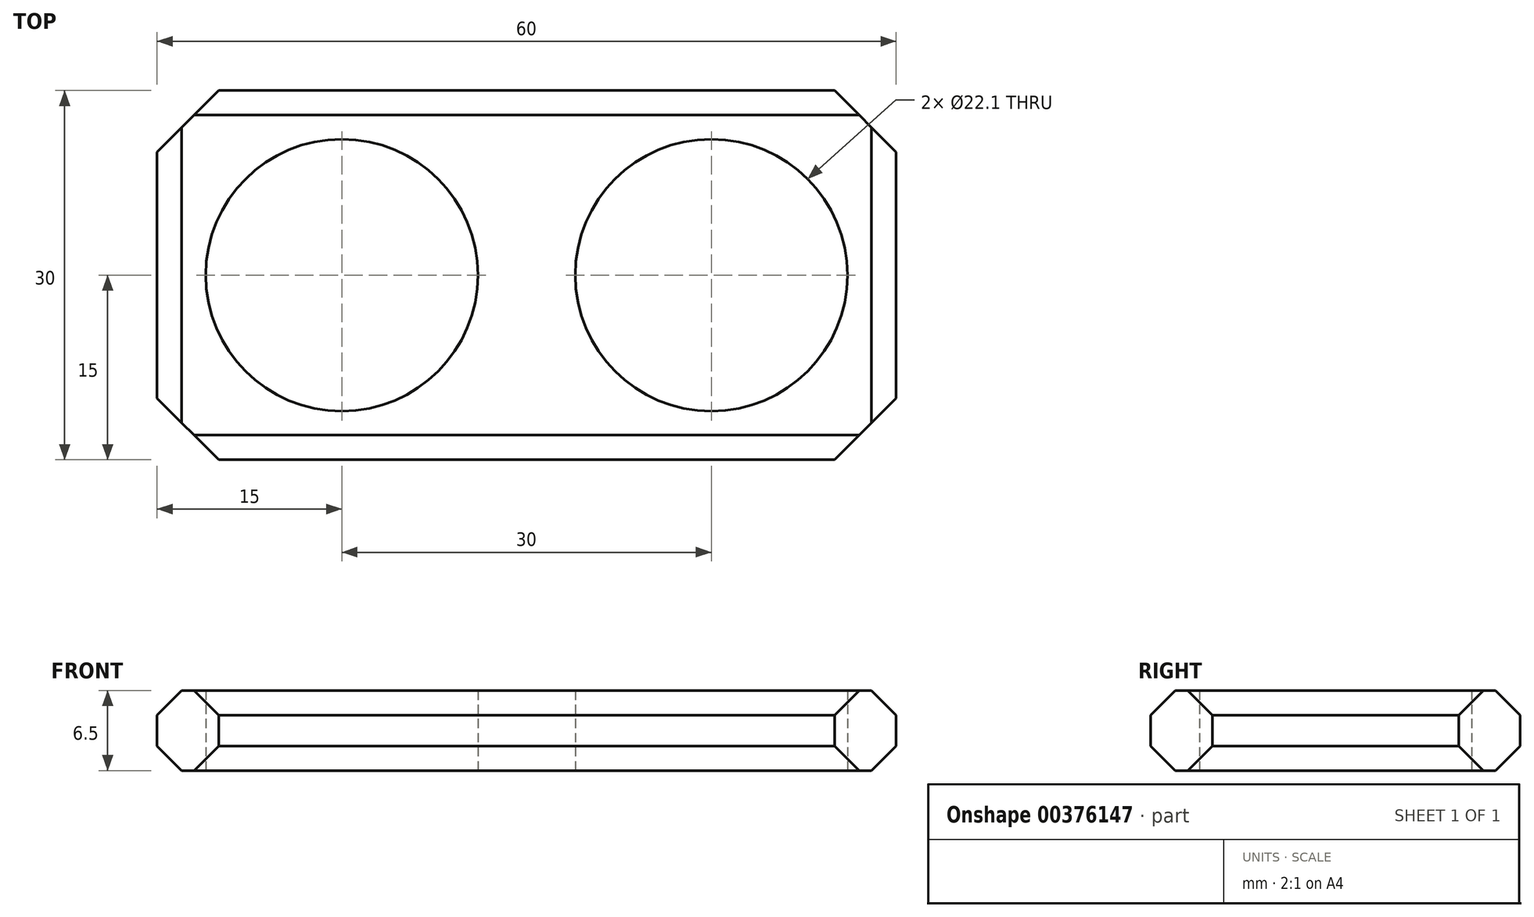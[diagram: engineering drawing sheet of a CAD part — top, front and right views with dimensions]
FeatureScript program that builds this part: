
annotation { "Feature Type Name" : "Feature", "Feature Type Description" : "" }
export const myFeature = defineFeature(function(context is Context, id is Id, definition is map)
    precondition{}
    {
        {
            var Q0;
            Q0=qCreatedBy(makeId("Top.planeOp"),FACE);
            var sketch = newSketch(context, id + "F0", { "sketchPlane" : qUnion([Q0])});
            skLineSegment(sketch, "E0.bottom", {"start": v(30, 15) * mm, "end": v(-30, 15) * mm});
            skLineSegment(sketch, "E0.top", {"start": v(30, -15) * mm, "end": v(-30, -15) * mm});
            skLineSegment(sketch, "E0.left", {"start": v(30, 15) * mm, "end": v(30, -15) * mm});
            skLineSegment(sketch, "E0.right", {"start": v(-30, 15) * mm, "end": v(-30, -15) * mm});
            skPoint(sketch, "E0.middle", {"position": v(0, 0) * mm});
            skLineSegment(sketch, "E1", {"start": v(-30, 0) * mm, "end": v(-15, 0) * mm});
            skPoint(sketch, "E1.endSnap0", {"position": v(-30, 0) * mm});
            skCircle(sketch, "E2", {"center": v(-15, 0) * mm, "radius": 11.05 * mm});
            skLineSegment(sketch, "E3", {"start": v(30, 0) * mm, "end": v(15, 0) * mm});
            skPoint(sketch, "E3.endSnap0", {"position": v(30, 0) * mm});
            skCircle(sketch, "E4", {"center": v(15, 0) * mm, "radius": 11.05 * mm});
            skSolve(sketch);
        }
        {
            var Q0;
            {var subQ3=sQuery(id+"F0.wireOp",EDGE,"E0.bottom");Q0=makeQuery(id+"F0.imprint","IMPRINT",FACE,{"disambiguationData":[TD([[makeQuery(id+"F0.imprint","IMPRINT",EDGE,{"derivedFrom":subQ3}),1.0]])]});}
            extrude(context, id + "F1", {"entities" : qUnion([Q0]), "depth" : 6.5 * mm});
        }
        {
            var Q0;
            Q0=makeQuery(id+"F1.opExtrude","CAP_EDGE",EDGE,{"disambiguationData":[OSD([sQuery(id+"F0.wireOp",EDGE,"E0.right")])],"isStart":false});
            var Q1;
            Q1=makeQuery(id+"F1.opExtrude","CAP_EDGE",EDGE,{"disambiguationData":[OSD([sQuery(id+"F0.wireOp",EDGE,"E0.right")])],"isStart":true});
            var Q2;
            Q2=makeQuery(id+"F1.opExtrude","CAP_EDGE",EDGE,{"disambiguationData":[OSD([sQuery(id+"F0.wireOp",EDGE,"E0.top")])],"isStart":true});
            var Q3;
            Q3=makeQuery(id+"F1.opExtrude","CAP_EDGE",EDGE,{"disambiguationData":[OSD([sQuery(id+"F0.wireOp",EDGE,"E0.top")])],"isStart":false});
            var Q4;
            Q4=makeQuery(id+"F1.opExtrude","CAP_EDGE",EDGE,{"disambiguationData":[OSD([sQuery(id+"F0.wireOp",EDGE,"E0.bottom")])],"isStart":true});
            var Q5;
            Q5=makeQuery(id+"F1.opExtrude","CAP_EDGE",EDGE,{"disambiguationData":[OSD([sQuery(id+"F0.wireOp",EDGE,"E0.bottom")])],"isStart":false});
            var Q6;
            Q6=makeQuery(id+"F1.opExtrude","CAP_EDGE",EDGE,{"disambiguationData":[OSD([sQuery(id+"F0.wireOp",EDGE,"E0.left")])],"isStart":true});
            var Q7;
            Q7=makeQuery(id+"F1.opExtrude","CAP_EDGE",EDGE,{"disambiguationData":[OSD([sQuery(id+"F0.wireOp",EDGE,"E0.left")])],"isStart":false});
            chamfer(context, id + "F2", {"entities" : qUnion([Q0, Q1, Q2, Q3, Q4, Q5, Q6, Q7]), "width" : 2 * mm, "tangentPropagation" : true});
        }
        {
            var Q0;
            Q0=makeQuery(id+"F1.opExtrude","SWEPT_EDGE",EDGE,{"disambiguationData":[OSD([sQuery(id+"F0.wireOp",EDGE,"E0.bottom"),sQuery(id+"F0.wireOp",EDGE,"E0.left")])]});
            var Q1;
            Q1=makeQuery(id+"F1.opExtrude","SWEPT_EDGE",EDGE,{"disambiguationData":[OSD([sQuery(id+"F0.wireOp",EDGE,"E0.top"),sQuery(id+"F0.wireOp",EDGE,"E0.left")])]});
            var Q2;
            Q2=makeQuery(id+"F1.opExtrude","SWEPT_EDGE",EDGE,{"disambiguationData":[OSD([sQuery(id+"F0.wireOp",EDGE,"E0.bottom"),sQuery(id+"F0.wireOp",EDGE,"E0.right")])]});
            var Q3;
            Q3=makeQuery(id+"F1.opExtrude","SWEPT_EDGE",EDGE,{"disambiguationData":[OSD([sQuery(id+"F0.wireOp",EDGE,"E0.top"),sQuery(id+"F0.wireOp",EDGE,"E0.right")])]});
            chamfer(context, id + "F3", {"entities" : qUnion([Q0, Q1, Q2, Q3]), "width" : 5 * mm, "tangentPropagation" : true});
        }
    });
